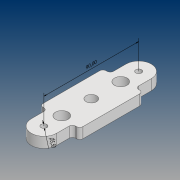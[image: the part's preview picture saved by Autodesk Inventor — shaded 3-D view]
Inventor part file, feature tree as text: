
AUTODESK INVENTOR PART (.ipt)
format: ipt  version: 2021 (Build 250183000, 183)  size: 147,968 bytes
history: native  units: mm
features: sketch x4, other x3, extrude x2, hole x2, fillet x1, projected_geometry x1
ambient origin geometry x8: Origin, YZ Plane, XZ Plane, XY Plane, X Axis, Y Axis, Z Axis, Center Point
bodies: Solid1 (feature_tree)
feature tree (13):
  other  "Annotations"
  extrude  "Extrusion1"  Depth=60.0mm
  hole  "Hole1"  [1 undecoded]
  fillet  "Fillet1"  Radius=10.0mm
  hole  "Hole2"  [1 undecoded]
  extrude  "Extrusion2"  Depth=6.0mm
  sketch  "Sketch1"  dims[d0=60.0mm d1=110.0mm]
  sketch  "Sketch2"  dims[d2=12.0mm d3=38.0mm d4=10.0mm d5=0.0mm]
  projected_geometry  "Projected Loop1"
  sketch  "Sketch3"  dims[d6=56.0mm]
  sketch  "Sketch4"  dims[d7=12.0mm d8=6.0mm d9=4.0mm d10=2.0mm d11=90.0deg d12=8.0mm d13=20.594885mm d14=3.0mm d15=5.5mm d16=6.0mm d17=4.0mm d18=2.0mm d19=90.0deg d20=8.0mm d21=20.594885mm d22=6.0mm d23=7.5mm d24=0.0mm d25=117.616421mm d26=118.351598mm d27=110.0mm d28=18.385343mm d29=5.5mm]
  other  "Linear Dimension 1"
  other  "Diameter Dimension 1"
note: 2 required parameter values undecoded (feature->parameter linkage not recoverable at this tier; creation-order binding heuristic only, values carry confidence <= 0.55)
